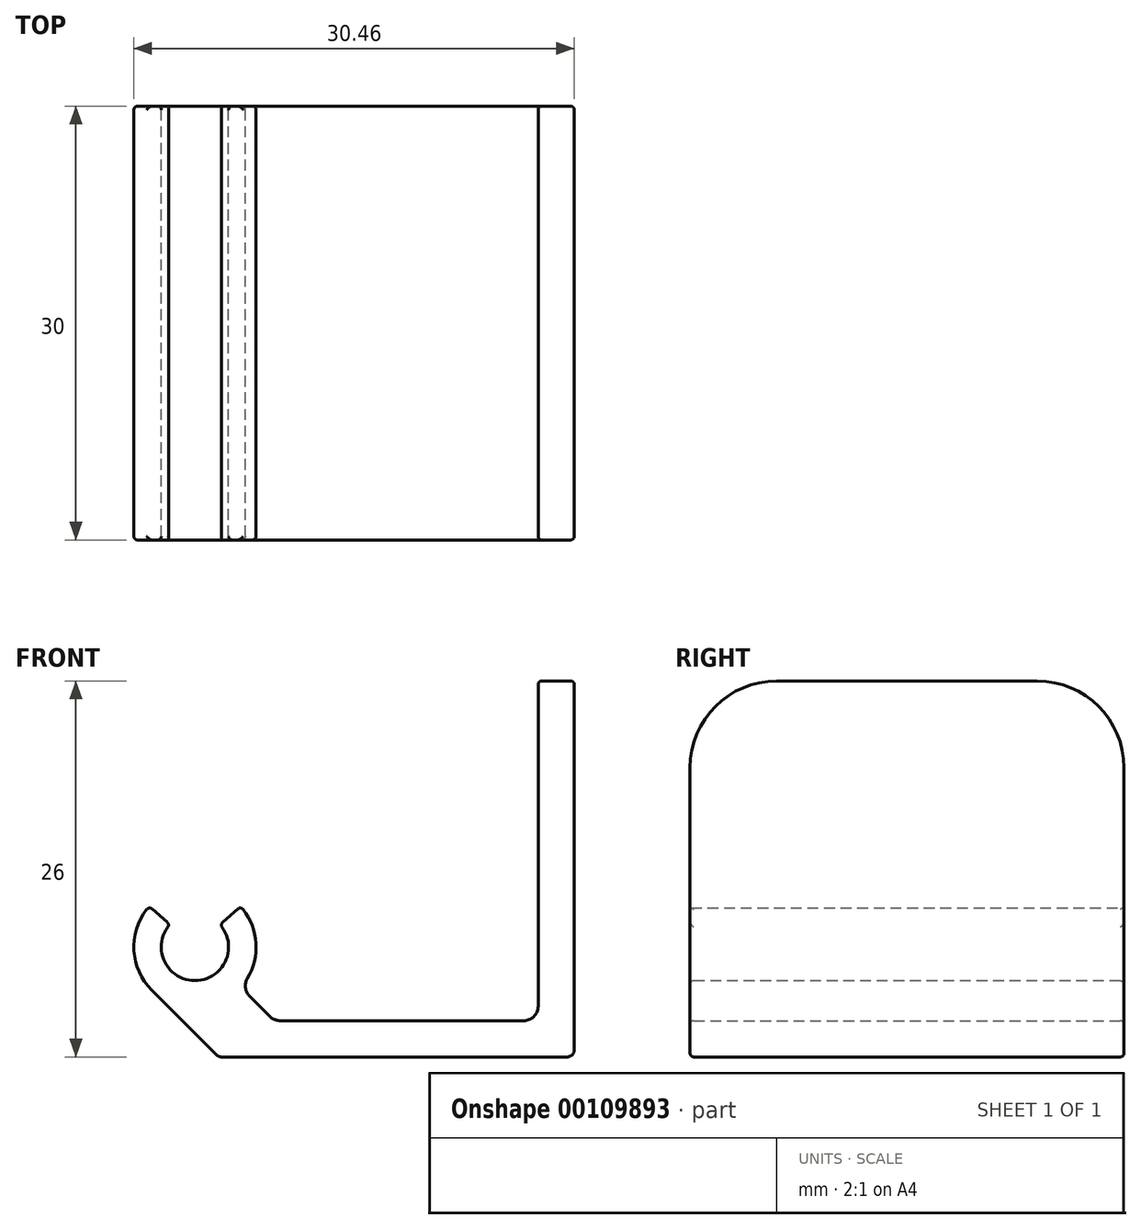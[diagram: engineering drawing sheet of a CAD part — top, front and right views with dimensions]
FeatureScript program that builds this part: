
annotation { "Feature Type Name" : "Feature", "Feature Type Description" : "" }
export const myFeature = defineFeature(function(context is Context, id is Id, definition is map)
    precondition{}
    {
        {
            var Q0;
            Q0=qCreatedBy(makeId("Front.planeOp"),FACE);
            var sketch = newSketch(context, id + "F0", { "sketchPlane" : qUnion([Q0])});
            skArc(sketch, "E0", {"start": v(-1.74, 1.54) * mm, "mid": v(0, -2.33) * mm, "end": v(1.74, 1.54) * mm});
            skArc(sketch, "E1", {"start": v(3.18, -2.79) * mm, "mid": v(4.22, 0.01) * mm, "end": v(3.16, 2.8) * mm});
            skLineSegment(sketch, "E2", {"start": v(-2.99, -2.99) * mm, "end": v(1.62, -7.6) * mm});
            skLineSegment(sketch, "E3", {"start": v(1.62, -7.6) * mm, "end": v(26.22, -7.6) * mm});
            skLineSegment(sketch, "E4", {"start": v(26.22, -7.6) * mm, "end": v(26.22, 18.4) * mm});
            skLineSegment(sketch, "E5", {"start": v(26.22, 18.4) * mm, "end": v(23.73, 18.4) * mm});
            skLineSegment(sketch, "E6", {"start": v(23.72, 18.4) * mm, "end": v(23.72, -5.1) * mm});
            skLineSegment(sketch, "E7", {"start": v(23.73, -5.1) * mm, "end": v(5.49, -5.1) * mm});
            skLineSegment(sketch, "E8", {"start": v(5.49, -5.1) * mm, "end": v(3.18, -2.79) * mm});
            skLineSegment(sketch, "E9", {"start": v(-1.74, 1.54) * mm, "end": v(-3.16, 2.8) * mm});
            skLineSegment(sketch, "E10", {"start": v(1.74, 1.54) * mm, "end": v(3.16, 2.8) * mm});
            skArc(sketch, "E11.trimOffspring", {"start": v(-3.16, 2.8) * mm, "mid": v(-4.22, -0.12) * mm, "end": v(-2.99, -2.99) * mm});
            skSolve(sketch);
        }
        {
            var Q0;
            Q0 = qSketchRegion(id + "F0", true);
            extrude(context, id + "F1", {"entities" : qUnion([Q0]), "depth" : 30 * mm});
        }
        {
            var Q0;
            Q0=makeQuery(id+"F1.opExtrude","CAP_EDGE",EDGE,{"disambiguationData":[OSD([sQuery(id+"F0.wireOp",EDGE,"E5")])],"isStart":false});
            var Q1;
            Q1=makeQuery(id+"F1.opExtrude","CAP_EDGE",EDGE,{"disambiguationData":[OSD([sQuery(id+"F0.wireOp",EDGE,"E5")])],"isStart":true});
            fillet(context, id + "F2", {"entities" : qUnion([Q0, Q1]), "radius" : 6 * mm, "tangentPropagation" : true, "allowEdgeOverflow" : false});
        }
        {
            var Q0;
            Q0=makeQuery(id+"F1.opExtrude","SWEPT_EDGE",EDGE,{"disambiguationData":[OSD([sQuery(id+"F0.wireOp",EDGE,"E6"),sQuery(id+"F0.wireOp",EDGE,"E7")])]});
            var Q1;
            Q1=makeQuery(id+"F1.opExtrude","SWEPT_EDGE",EDGE,{"disambiguationData":[OSD([sQuery(id+"F0.wireOp",EDGE,"E7"),sQuery(id+"F0.wireOp",EDGE,"E8")])]});
            var Q2;
            Q2=makeQuery(id+"F1.opExtrude","SWEPT_EDGE",EDGE,{"disambiguationData":[OSD([sQuery(id+"F0.wireOp",EDGE,"E1"),sQuery(id+"F0.wireOp",EDGE,"E8")])]});
            fillet(context, id + "F3", {"entities" : qUnion([Q0, Q1, Q2]), "radius" : 1 * mm, "tangentPropagation" : true, "allowEdgeOverflow" : false});
        }
        {
            var Q0;
            Q0=makeQuery(id+"F1.opExtrude","SWEPT_EDGE",EDGE,{"disambiguationData":[OSD([sQuery(id+"F0.wireOp",EDGE,"E3"),sQuery(id+"F0.wireOp",EDGE,"E4")])]});
            var Q1;
            Q1=makeQuery(id+"F1.opExtrude","SWEPT_EDGE",EDGE,{"disambiguationData":[OSD([sQuery(id+"F0.wireOp",EDGE,"E2"),sQuery(id+"F0.wireOp",EDGE,"E3")])]});
            fillet(context, id + "F4", {"entities" : qUnion([Q0, Q1]), "radius" : .5 * mm, "tangentPropagation" : true, "allowEdgeOverflow" : false});
        }
        {
            var Q0;
            Q0=makeQuery(id+"F1.opExtrude","SWEPT_EDGE",EDGE,{"disambiguationData":[OSD([sQuery(id+"F0.wireOp",EDGE,"E0"),sQuery(id+"F0.wireOp",EDGE,"E9")])]});
            var Q1;
            Q1=makeQuery(id+"F1.opExtrude","SWEPT_EDGE",EDGE,{"disambiguationData":[OSD([sQuery(id+"F0.wireOp",EDGE,"E9"),sQuery(id+"F0.wireOp",EDGE,"E11.trimOffspring")])]});
            var Q2;
            Q2=makeQuery(id+"F1.opExtrude","SWEPT_EDGE",EDGE,{"disambiguationData":[OSD([sQuery(id+"F0.wireOp",EDGE,"E0"),sQuery(id+"F0.wireOp",EDGE,"E10")])]});
            var Q3;
            Q3=makeQuery(id+"F1.opExtrude","SWEPT_EDGE",EDGE,{"disambiguationData":[OSD([sQuery(id+"F0.wireOp",EDGE,"E1"),sQuery(id+"F0.wireOp",EDGE,"E10")])]});
            var Q4;
            Q4=makeQuery(id+"F1.opExtrude","CAP_EDGE",EDGE,{"disambiguationData":[OSD([sQuery(id+"F0.wireOp",EDGE,"E1")])],"isStart":false});
            var Q5;
            Q5=makeQuery(id+"F1.opExtrude","CAP_EDGE",EDGE,{"disambiguationData":[OSD([sQuery(id+"F0.wireOp",EDGE,"E11.trimOffspring")])],"isStart":false});
            var Q6;
            Q6=makeQuery(id+"F1.opExtrude","CAP_EDGE",EDGE,{"disambiguationData":[OSD([sQuery(id+"F0.wireOp",EDGE,"E0")])],"isStart":false});
            var Q7;
            Q7=makeQuery(id+"F1.opExtrude","CAP_EDGE",EDGE,{"disambiguationData":[OSD([sQuery(id+"F0.wireOp",EDGE,"E0")])],"isStart":true});
            fillet(context, id + "F5", {"entities" : qUnion([Q0, Q1, Q2, Q3, Q4, Q5, Q6, Q7]), "radius" : .25 * mm, "tangentPropagation" : true, "allowEdgeOverflow" : false});
        }
    });
